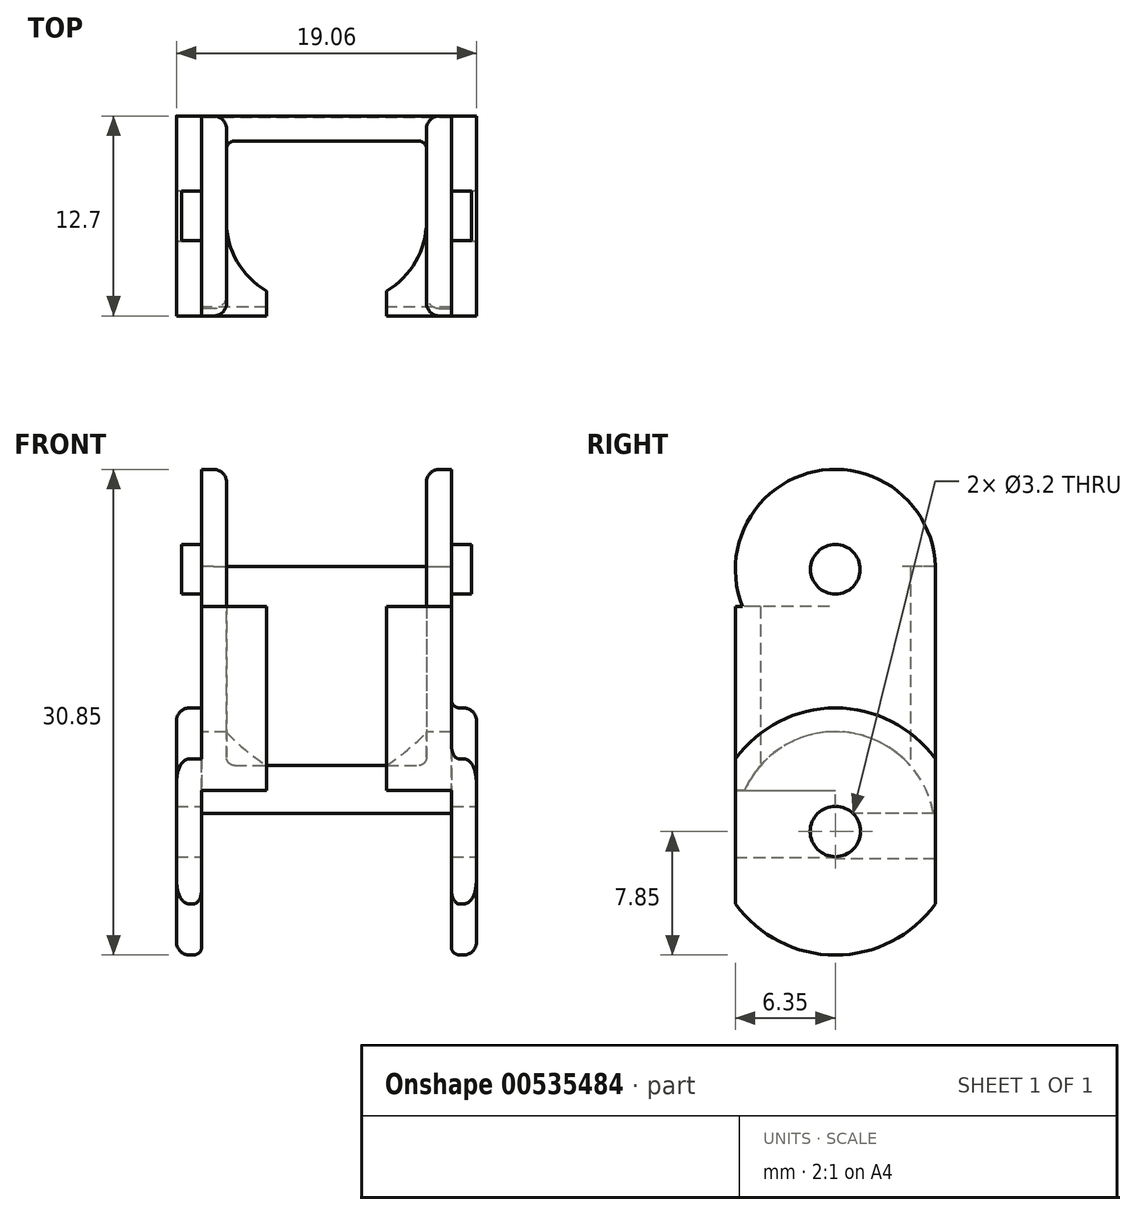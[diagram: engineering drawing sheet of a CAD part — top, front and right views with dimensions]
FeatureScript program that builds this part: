
annotation { "Feature Type Name" : "Feature", "Feature Type Description" : "" }
export const myFeature = defineFeature(function(context is Context, id is Id, definition is map)
    precondition{}
    {
        {
            var Q0;
            Q0=qCreatedBy(makeId("Top.planeOp"),FACE);
            var sketch = newSketch(context, id + "F0", { "sketchPlane" : qUnion([Q0])});
            skLineSegment(sketch, "E0.bottom", {"start": v(-7.94, 6.35) * mm, "end": v(7.94, 6.35) * mm});
            skLineSegment(sketch, "E0.top", {"start": v(-7.94, -6.35) * mm, "end": v(-3.81, -6.35) * mm});
            skLineSegment(sketch, "E0.left", {"start": v(-7.94, 6.35) * mm, "end": v(-7.94, -6.35) * mm});
            skLineSegment(sketch, "E0.right", {"start": v(7.94, 6.35) * mm, "end": v(7.94, -6.35) * mm});
            skPoint(sketch, "E0.middle", {"position": v(0, 0) * mm});
            skLineSegment(sketch, "E1.bottom", {"start": v(-6.35, 4.76) * mm, "end": v(6.35, 4.76) * mm});
            skLineSegment(sketch, "E1.top", {"start": v(-6.35, -4.76) * mm, "end": v(-3.81, -4.76) * mm});
            skLineSegment(sketch, "E1.left", {"start": v(-6.35, 4.76) * mm, "end": v(-6.35, -4.76) * mm});
            skLineSegment(sketch, "E1.right", {"start": v(6.35, 4.76) * mm, "end": v(6.35, -4.76) * mm});
            skLineSegment(sketch, "E2", {"start": v(-3.81, -4.76) * mm, "end": v(-3.81, -6.35) * mm});
            skLineSegment(sketch, "E3", {"start": v(3.81, -4.76) * mm, "end": v(3.81, -6.35) * mm});
            skLineSegment(sketch, "E4.trimOffspring", {"start": v(3.8, -6.35) * mm, "end": v(7.94, -6.35) * mm});
            skLineSegment(sketch, "E5.trimOffspring", {"start": v(3.8, -4.76) * mm, "end": v(6.35, -4.76) * mm});
            skSolve(sketch);
        }
        {
            var Q0;
            Q0=makeQuery(id+"F0.imprint","IMPRINT",FACE,{"disambiguationData":[TD([[makeQuery(id+"F0.imprint","IMPRINT",EDGE,{"derivedFrom":sQuery(id+"F0.wireOp",EDGE,"E0.bottom")}),-1.0]])]});
            extrude(context, id + "F1", {"entities" : qUnion([Q0]), "depth" : 14.29 * mm, "offsetDistance" : 25.4 * mm});
        }
        {
            var Q0;
            Q0=makeQuery(id+"F1.opExtrude","SWEPT_FACE",FACE,{"disambiguationData":[OSD([sQuery(id+"F0.wireOp",EDGE,"E0.right")])]});
            var sketch = newSketch(context, id + "F2", { "sketchPlane" : qUnion([Q0])});
            skCircle(sketch, "E6", {"center": v(0, 0) * mm, "radius": 6.35 * mm, "construction": true});
            skCircle(sketch, "E7", {"center": v(0, 16.65) * mm, "radius": 6.35 * mm});
            skSolve(sketch);
        }
        {
            var Q0;
            {var subQ1=sQuery(id+"F0.wireOp",EDGE,"E0.right");var subQ2=makeQuery(id+"F1.opExtrude","CAP_EDGE",EDGE,{"disambiguationData":[OSD([subQ1])],"isStart":false});Q0=makeQuery(id+"F2.imprint","IMPRINT",FACE,{"disambiguationData":[TD([[makeQuery(id+"F2.imprint","IMPRINT",EDGE,{"derivedFrom":subQ2}),-1.0]])]});}
            var Q1;
            Q1=makeQuery(id+"F1.opExtrude","SWEPT_FACE",FACE,{"disambiguationData":[OSD([sQuery(id+"F0.wireOp",EDGE,"E1.right")])]});
            extrude(context, id + "F3", {"entities" : qUnion([Q0]), "operationType" : NewBodyOperationType.ADD, "oppositeDirection" : true, "depth" : 1.59 * mm, "endBoundEntityFace" : qUnion([Q1]), "offsetDistance" : 25.4 * mm});
        }
        {
            var Q0;
            Q0=makeQuery(id+"F3.boolean.opBoolean","MERGE",FACE,{"derivedFrom":[makeQuery(id+"F1.opExtrude","SWEPT_FACE",FACE,{"disambiguationData":[OSD([sQuery(id+"F0.wireOp",EDGE,"E0.right")])]}),makeQuery(id+"F3.opExtrude","CAP_FACE",FACE,{"disambiguationData":[OSD([sQuery(id+"F2.wireOp",EDGE,"E7")])],"isStart":true})]});
            var sketch = newSketch(context, id + "F4", { "sketchPlane" : qUnion([Q0])});
            skCircle(sketch, "E8", {"center": v(0, 0) * mm, "radius": 7.85 * mm});
            skSolve(sketch);
        }
        {
            var Q0;
            Q0 = qSketchRegion(id + "F4", true);
            extrude(context, id + "F5", {"entities" : qUnion([Q0]), "operationType" : NewBodyOperationType.ADD, "depth" : 1.59 * mm, "offsetDistance" : 25.4 * mm});
        }
        {
            var Q0;
            Q0=makeQuery(id+"F1.opExtrude","SWEPT_BODY",BODY,{"disambiguationData":[OSD([sQuery(id+"F0.wireOp",EDGE,"E0.bottom"),sQuery(id+"F0.wireOp",EDGE,"E0.top"),sQuery(id+"F0.wireOp",EDGE,"E0.left"),sQuery(id+"F0.wireOp",EDGE,"E0.right"),sQuery(id+"F0.wireOp",EDGE,"E1.bottom"),sQuery(id+"F0.wireOp",EDGE,"E1.top"),sQuery(id+"F0.wireOp",EDGE,"E1.left"),sQuery(id+"F0.wireOp",EDGE,"E1.right"),sQuery(id+"F0.wireOp",EDGE,"E2"),sQuery(id+"F0.wireOp",EDGE,"E3"),sQuery(id+"F0.wireOp",EDGE,"E4.trimOffspring"),sQuery(id+"F0.wireOp",EDGE,"E5.trimOffspring")])]});
            var Q1;
            Q1=qCreatedBy(makeId("Right.planeOp"),FACE);
            mirror(context, id + "F6", {"operationType" : NewBodyOperationType.ADD, "entities" : qUnion([Q0]), "mirrorPlane" : qUnion([Q1])});
        }
        {
            var Q0;
            {var subQ0=sQuery(id+"F0.wireOp",EDGE,"E1.right");Q0=makeQuery(id+"F3.boolean.opBoolean","MERGE",FACE,{"derivedFrom":[makeQuery(id+"F1.opExtrude","SWEPT_FACE",FACE,{"disambiguationData":[OSD([subQ0])]}),makeQuery(id+"F3.opExtrude","CAP_FACE",FACE,{"disambiguationData":[OSD([subQ0])],"isStart":false})]});}
            var sketch = newSketch(context, id + "F7", { "sketchPlane" : qUnion([Q0])});
            skCircle(sketch, "E9", {"center": v(0, 0) * mm, "radius": 6.34 * mm});
            skSolve(sketch);
        }
        {
            var Q0;
            Q0 = qSketchRegion(id + "F7", true);
            var Q1;
            Q1=makeQuery(id+"F5.opExtrude","CAP_FACE",FACE,{"disambiguationData":[OSD([sQuery(id+"F4.wireOp",EDGE,"E8")])],"isStart":true});
            var Q2;
            Q2=makeQuery(id+"F6.opPattern","COPY",FACE,{"derivedFrom":makeQuery(id+"F5.opExtrude","CAP_FACE",FACE,{"disambiguationData":[OSD([sQuery(id+"F4.wireOp",EDGE,"E8")])],"isStart":true}),"instanceName":"1"});
            extrude(context, id + "F8", {"entities" : qUnion([Q0]), "operationType" : NewBodyOperationType.REMOVE, "endBound" : BoundingType.UP_TO_SURFACE, "oppositeDirection" : true, "depth" : 25.4 * mm, "endBoundEntityFace" : qUnion([Q1]), "offsetDistance" : 25.4 * mm, "hasSecondDirection" : true, "secondDirectionBound" : SecondDirectionBoundingType.UP_TO_SURFACE, "secondDirectionOppositeDirection" : false, "secondDirectionDepth" : 25.4 * mm, "secondDirectionBoundEntityFace" : qUnion([Q2])});
        }
        {
            var Q0;
            Q0=qCreatedBy(makeId("Front.planeOp"),FACE);
            var sketch = newSketch(context, id + "F9", { "sketchPlane" : qUnion([Q0])});
            skLineSegment(sketch, "E10.bottom", {"start": v(-7.94, 0) * mm, "end": v(7.94, 0) * mm});
            skLineSegment(sketch, "E10.top", {"start": v(-7.94, 5.88) * mm, "end": v(7.94, 5.88) * mm});
            skLineSegment(sketch, "E10.left", {"start": v(-7.94, 0) * mm, "end": v(-7.94, 5.88) * mm});
            skLineSegment(sketch, "E10.right", {"start": v(7.94, 0) * mm, "end": v(7.94, 5.88) * mm});
            skSolve(sketch);
        }
        {
            var Q0;
            Q0=makeQuery(id+"F5.opExtrude","CAP_EDGE",EDGE,{"disambiguationData":[OSD([sQuery(id+"F4.wireOp",EDGE,"E8")])],"isStart":false});
            var Q1;
            Q1=makeQuery(id+"F3.opExtrude","CAP_EDGE",EDGE,{"disambiguationData":[OSD([sQuery(id+"F2.wireOp",EDGE,"E7")])],"isStart":false});
            var Q2;
            Q2=makeQuery(id+"F6.opPattern","COPY",EDGE,{"derivedFrom":makeQuery(id+"F5.opExtrude","CAP_EDGE",EDGE,{"disambiguationData":[OSD([sQuery(id+"F4.wireOp",EDGE,"E8")])],"isStart":false}),"instanceName":"1"});
            var Q3;
            Q3=makeQuery(id+"F6.opPattern","COPY",EDGE,{"derivedFrom":makeQuery(id+"F3.opExtrude","CAP_EDGE",EDGE,{"disambiguationData":[OSD([sQuery(id+"F2.wireOp",EDGE,"E7")])],"isStart":false}),"instanceName":"1"});
            fillet(context, id + "F10", {"entities" : qUnion([Q0, Q1, Q2, Q3]), "radius" : 0.81 * mm, "tangentPropagation" : true, "allowEdgeOverflow" : false});
        }
        {
            var Q0;
            Q0 = qSketchRegion(id + "F7", true);
            extrude(context, id + "F11", {"entities" : qUnion([Q0]), "operationType" : NewBodyOperationType.REMOVE, "oppositeDirection" : true, "depth" : 1.59 * mm, "offsetDistance" : 25.4 * mm, "hasSecondDirection" : true, "secondDirectionOppositeDirection" : false, "secondDirectionDepth" : 14.29 * mm});
        }
        {
            var Q0;
            Q0=makeQuery(id+"F9.imprint","IMPRINT",FACE,{"disambiguationData":[TD([[makeQuery(id+"F9.imprint","IMPRINT",EDGE,{"derivedFrom":sQuery(id+"F9.wireOp",EDGE,"E10.bottom")}),1.0]])]});
            extrude(context, id + "F12", {"entities" : qUnion([Q0]), "operationType" : NewBodyOperationType.REMOVE, "endBound" : BoundingType.SYMMETRIC, "oppositeDirection" : true, "depth" : 25.4 * mm, "offsetDistance" : 25.4 * mm, "hasSecondDirection" : true, "secondDirectionOppositeDirection" : true, "secondDirectionDepth" : 25.4 * mm});
        }
        {
            var Q0;
            {var subQ1=sQuery(id+"F0.wireOp",EDGE,"E0.right");var subQ3=sQuery(id+"F0.wireOp",EDGE,"E1.bottom");var subQ5=sQuery(id+"F0.wireOp",EDGE,"E1.left");var subQ10=sQuery(id+"F0.wireOp",EDGE,"E0.left");var subQ12=sQuery(id+"F0.wireOp",EDGE,"E1.right");var subQ14=sQuery(id+"F0.wireOp",EDGE,"E0.bottom");var subQ15=makeQuery(id+"F1.opExtrude","SWEPT_FACE",FACE,{"disambiguationData":[OSD([subQ14])]});var subQ16=sQuery(id+"F0.wireOp",EDGE,"E2");var subQ17=sQuery(id+"F0.wireOp",EDGE,"E1.top");var subQ18=sQuery(id+"F0.wireOp",EDGE,"E0.top");Q0=makeQuery(id+"FmwXntm0pgXdfj9_1.boolean.opBoolean","SPLIT",FACE,{"disambiguationData":[TD([subQ15])],"derivedFrom":makeQuery(id+"F3.boolean.opBoolean","SPLIT",FACE,{"disambiguationData":[TD([subQ15])],"derivedFrom":makeQuery(id+"F1.opExtrude","CAP_FACE",FACE,{"disambiguationData":[OSD([subQ14,subQ18,subQ10,subQ1,subQ3,subQ17,subQ5,subQ12,subQ16,sQuery(id+"F0.wireOp",EDGE,"E3"),sQuery(id+"F0.wireOp",EDGE,"E4.trimOffspring"),sQuery(id+"F0.wireOp",EDGE,"E5.trimOffspring")])],"isStart":false})})});}
            var sketch = newSketch(context, id + "F13", { "sketchPlane" : qUnion([Q0])});
            skLineSegment(sketch, "E11.bottom", {"start": v(7.94, 4.76) * mm, "end": v(-7.94, 4.76) * mm});
            skLineSegment(sketch, "E11.top", {"start": v(7.94, 6.35) * mm, "end": v(-7.94, 6.35) * mm});
            skLineSegment(sketch, "E11.left", {"start": v(7.94, 4.76) * mm, "end": v(7.94, 6.35) * mm});
            skLineSegment(sketch, "E11.right", {"start": v(-7.94, 4.76) * mm, "end": v(-7.94, 6.35) * mm});
            skSolve(sketch);
        }
        {
            var Q0;
            Q0 = qSketchRegion(id + "F13", true);
            var Q1;
            {var subQ0=sQuery(id+"F7.wireOp",EDGE,"E9");var subQ2=sQuery(id+"F0.wireOp",EDGE,"E1.left");var subQ3=sQuery(id+"F0.wireOp",EDGE,"E2");var subQ6=sQuery(id+"F0.wireOp",EDGE,"E1.top");var subQ8=sQuery(id+"F0.wireOp",EDGE,"E0.bottom");var subQ9=sQuery(id+"F0.wireOp",EDGE,"E0.top");var subQ10=sQuery(id+"F0.wireOp",EDGE,"E0.left");var subQ11=sQuery(id+"F0.wireOp",EDGE,"E1.bottom");var subQ13=sQuery(id+"F0.wireOp",EDGE,"E5.trimOffspring");var subQ14=sQuery(id+"F0.wireOp",EDGE,"E4.trimOffspring");var subQ15=sQuery(id+"F0.wireOp",EDGE,"E3");var subQ16=makeQuery(id+"F1.opExtrude","CAP_FACE",FACE,{"disambiguationData":[OSD([subQ8,subQ9,subQ10,sQuery(id+"F0.wireOp",EDGE,"E0.right"),subQ11,subQ6,subQ2,sQuery(id+"F0.wireOp",EDGE,"E1.right"),subQ3,subQ15,subQ14,subQ13])],"isStart":true});var subQ17=makeQuery(id+"F8.boolean.opBoolean","SPLIT",FACE,{"disambiguationData":[TD([makeQuery(id+"F1.opExtrude","SWEPT_FACE",FACE,{"disambiguationData":[OSD([subQ8])]})])],"derivedFrom":subQ16});Q1=makeQuery(id+"F11.boolean.opBoolean","INTERSECT",VERTEX,{"disambiguationData":[OD(0.0)],"derivedFrom":[makeQuery(id+"FmwXntm0pgXdfj9_1.boolean.opBoolean","MERGE",FACE,{"derivedFrom":[subQ17,makeQuery(id+"F8.boolean.opBoolean","SPLIT",FACE,{"disambiguationData":[TD([makeQuery(id+"F1.opExtrude","SWEPT_FACE",FACE,{"disambiguationData":[OSD([subQ15])]})])],"derivedFrom":subQ16}),makeQuery(id+"FmwXntm0pgXdfj9_1.opPattern","COPY",FACE,{"derivedFrom":subQ17,"instanceName":"1"})]}),makeQuery(id+"F11.opExtrude","SWEPT_FACE",FACE,{"disambiguationData":[OSD([subQ0])]})]});}
            extrude(context, id + "F14", {"entities" : qUnion([Q0]), "operationType" : NewBodyOperationType.ADD, "depth" : 2.54 * mm, "endBoundEntityVertex" : qUnion([Q1]), "offsetDistance" : 25.4 * mm});
        }
        {
            var Q0;
            {var subQ0=sQuery(id+"F4.wireOp",EDGE,"E8");Q0=makeQuery(id+"F4vwekiissYTjzZ_1.boolean.opBoolean","MERGE",FACE,{"derivedFrom":[makeQuery(id+"F12.boolean.opBoolean","MERGE",FACE,{"derivedFrom":[makeQuery(id+"F11.boolean.opBoolean","MERGE",FACE,{"derivedFrom":[makeQuery(id+"F8.boolean.opBoolean","MERGE",FACE,{"derivedFrom":[makeQuery(id+"F5.opExtrude","CAP_FACE",FACE,{"disambiguationData":[OSD([subQ0])],"isStart":true}),makeQuery(id+"F8.opExtrude","CAP_FACE",FACE,{"disambiguationData":[OSD([subQ0])],"isStart":false})]}),makeQuery(id+"F11.opExtrude","CAP_FACE",FACE,{"disambiguationData":[OSD([sQuery(id+"F7.wireOp",EDGE,"E9")])],"isStart":false})]}),makeQuery(id+"F12.opExtrude","SWEPT_FACE",FACE,{"disambiguationData":[OSD([sQuery(id+"F9.wireOp",EDGE,"E10.right")])]})]}),makeQuery(id+"F4vwekiissYTjzZ_1.opExtrude","CAP_FACE",FACE,{"disambiguationData":[OSD([sQuery(id+"F27.wireOp",EDGE,"E23")])],"isStart":true})]});}
            var sketch = newSketch(context, id + "F15", { "sketchPlane" : qUnion([Q0])});
            skCircle(sketch, "E12", {"center": v(0, 0) * mm, "radius": 1.6 * mm});
            skSolve(sketch);
        }
        {
            var Q0;
            Q0 = qSketchRegion(id + "F15", true);
            extrude(context, id + "F16", {"entities" : qUnion([Q0]), "operationType" : NewBodyOperationType.REMOVE, "depth" : 25.4 * mm, "offsetDistance" : 25.4 * mm, "hasSecondDirection" : true, "secondDirectionOppositeDirection" : true, "secondDirectionDepth" : 25.4 * mm});
        }
        {
            var Q0;
            {var subQ0=sQuery(id+"F0.wireOp",EDGE,"E0.right");Q0=makeQuery(id+"FuRak2iaO5MuixO_1.boolean.opBoolean","MERGE",FACE,{"derivedFrom":[makeQuery(id+"F14.boolean.opBoolean","MERGE",FACE,{"derivedFrom":[makeQuery(id+"F3.boolean.opBoolean","MERGE",FACE,{"derivedFrom":[makeQuery(id+"F1.opExtrude","SWEPT_FACE",FACE,{"disambiguationData":[OSD([subQ0])]}),makeQuery(id+"F3.opExtrude","CAP_FACE",FACE,{"disambiguationData":[OSD([subQ0,sQuery(id+"F2.wireOp",EDGE,"E7")])],"isStart":true})]}),makeQuery(id+"F14.opExtrude","SWEPT_FACE",FACE,{"disambiguationData":[OSD([sQuery(id+"F9.wireOp",EDGE,"E10.top"),sQuery(id+"F9.wireOp",EDGE,"E10.right")])]})]}),makeQuery(id+"FuRak2iaO5MuixO_1.opExtrude","SWEPT_FACE",FACE,{"disambiguationData":[OSD([sQuery(id+"F13.wireOp",EDGE,"E11.left")])]})]});}
            var sketch = newSketch(context, id + "F17", { "sketchPlane" : qUnion([Q0])});
            skCircle(sketch, "E13", {"center": v(0, 16.65) * mm, "radius": 1.57 * mm});
            skSolve(sketch);
        }
        {
            var Q0;
            Q0=makeQuery(id+"F17.imprint","IMPRINT",FACE,{"disambiguationData":[TD([[makeQuery(id+"F17.imprint","IMPRINT",EDGE,{"derivedFrom":sQuery(id+"F17.wireOp",EDGE,"E13")}),1.0]])]});
            extrude(context, id + "F18", {"entities" : qUnion([Q0]), "operationType" : NewBodyOperationType.ADD, "depth" : 1.27 * mm, "offsetDistance" : 25.4 * mm});
        }
        {
            var Q0;
            {var subQ0=sQuery(id+"F0.wireOp",EDGE,"E0.right");var subQ1=makeQuery(id+"FmwXntm0pgXdfj9_1.opPattern","COPY",FACE,{"derivedFrom":makeQuery(id+"F3.boolean.opBoolean","MERGE",FACE,{"derivedFrom":[makeQuery(id+"F1.opExtrude","SWEPT_FACE",FACE,{"disambiguationData":[OSD([subQ0])]}),makeQuery(id+"F3.opExtrude","CAP_FACE",FACE,{"disambiguationData":[OSD([subQ0,sQuery(id+"F2.wireOp",EDGE,"E7")])],"isStart":true})]}),"instanceName":"1"});var subQ2=makeQuery(id+"F1.opExtrude","SWEPT_FACE",FACE,{"disambiguationData":[OSD([sQuery(id+"F0.wireOp",EDGE,"E0.left")])]});var subQ3=sQuery(id+"F9.wireOp",EDGE,"E10.left");var subQ4=sQuery(id+"F9.wireOp",EDGE,"E10.top");var subQ5=makeQuery(id+"F12.opExtrude","SWEPT_FACE",FACE,{"disambiguationData":[OSD([subQ4])]});Q0=makeQuery(id+"FuRak2iaO5MuixO_1.boolean.opBoolean","MERGE",FACE,{"derivedFrom":[makeQuery(id+"F14.boolean.opBoolean","MERGE",FACE,{"derivedFrom":[makeQuery(id+"FmwXntm0pgXdfj9_1.boolean.opBoolean","MERGE",FACE,{"derivedFrom":[subQ2,subQ1]}),makeQuery(id+"F14.opExtrude","SWEPT_FACE",FACE,{"disambiguationData":[OSD([subQ4,subQ3]),TDD([makeQuery(id+"F12.boolean.opBoolean","COPY",EDGE,{"disambiguationData":[topologyDisambiguationEdgeConnected([subQ2,subQ1,subQ5]),TD([makeQuery(id+"F1.opExtrude","SWEPT_FACE",FACE,{"disambiguationData":[OSD([sQuery(id+"F0.wireOp",EDGE,"E0.bottom")])]})])],"derivedFrom":makeQuery(id+"F12.opExtrude","SWEPT_EDGE",EDGE,{"disambiguationData":[OSD([subQ4,subQ3])]})})])]})]}),makeQuery(id+"FuRak2iaO5MuixO_1.opExtrude","SWEPT_FACE",FACE,{"disambiguationData":[OSD([sQuery(id+"F13.wireOp",EDGE,"E11.right")])]})]});}
            var sketch = newSketch(context, id + "F19", { "sketchPlane" : qUnion([Q0])});
            skCircle(sketch, "E14", {"center": v(0, 16.65) * mm, "radius": 1.57 * mm});
            skSolve(sketch);
        }
        {
            var Q0;
            Q0 = qSketchRegion(id + "F19", true);
            extrude(context, id + "F20", {"entities" : qUnion([Q0]), "operationType" : NewBodyOperationType.ADD, "depth" : 1.27 * mm, "offsetDistance" : 25.4 * mm});
        }
        {
            var Q0;
            Q0=makeQuery(id+"F12.boolean.opBoolean","COPY",FACE,{"disambiguationData":[TD([makeQuery(id+"F1.opExtrude","SWEPT_FACE",FACE,{"disambiguationData":[OSD([sQuery(id+"F0.wireOp",EDGE,"E0.bottom")])]})])],"derivedFrom":makeQuery(id+"F12.opExtrude","SWEPT_FACE",FACE,{"disambiguationData":[OSD([sQuery(id+"F9.wireOp",EDGE,"E10.top")])]})});
            var Q1;
            Q1=makeQuery(id+"F14.opExtrude","CAP_VERTEX",VERTEX,{"disambiguationData":[OSD([sQuery(id+"F0.wireOp",EDGE,"E0.bottom"),sQuery(id+"F9.wireOp",EDGE,"E10.top"),sQuery(id+"F9.wireOp",EDGE,"E10.right"),dummyQuery(id+"F14.vertexPlane.planeOp",FACE)])],"isStart":false});
            extrude(context, id + "F21", {"entities" : qUnion([Q0]), "operationType" : NewBodyOperationType.ADD, "depth" : 5.08 * mm, "endBoundEntityVertex" : qUnion([Q1]), "offsetDistance" : 25.4 * mm});
        }
        {
            var Q0;
            Q0=makeQuery(id+"F1.opExtrude","SWEPT_EDGE",EDGE,{"disambiguationData":[OSD([sQuery(id+"F0.wireOp",EDGE,"E1.top"),sQuery(id+"F0.wireOp",EDGE,"E1.left")])]});
            fillet(context, id + "F22", {"entities" : qUnion([Q0]), "radius" : 5.08 * mm, "tangentPropagation" : true, "allowEdgeOverflow" : false});
        }
        {
            var Q0;
            {var subQ0=sQuery(id+"F0.wireOp",EDGE,"E5.trimOffspring");var subQ2=sQuery(id+"F0.wireOp",EDGE,"E1.right");var subQ3=makeQuery(id+"F1.opExtrude","SWEPT_EDGE",EDGE,{"disambiguationData":[OSD([subQ2,subQ0])]});Q0=makeQuery(id+"FmwXntm0pgXdfj9_1.boolean.opBoolean","MERGE",EDGE,{"derivedFrom":[makeQuery(id+"F8.boolean.opBoolean","SPLIT",EDGE,{"disambiguationData":[topologyDisambiguationEdgeConnected([makeQuery(id+"F1.opExtrude","SWEPT_FACE",FACE,{"disambiguationData":[OSD([subQ2])]})])],"derivedFrom":subQ3}),makeQuery(id+"F8.boolean.opBoolean","SPLIT",EDGE,{"disambiguationData":[topologyDisambiguationEdgeConnected([makeQuery(id+"F8.opExtrude","CAP_FACE",FACE,{"disambiguationData":[OSD([sQuery(id+"F7.wireOp",EDGE,"E9")])],"isStart":true})])],"derivedFrom":subQ3}),makeQuery(id+"FmwXntm0pgXdfj9_1.opPattern","COPY",EDGE,{"derivedFrom":makeQuery(id+"F1.opExtrude","SWEPT_EDGE",EDGE,{"disambiguationData":[OSD([sQuery(id+"F0.wireOp",EDGE,"E1.top"),sQuery(id+"F0.wireOp",EDGE,"E1.left")])]}),"instanceName":"1"})]});}
            fillet(context, id + "F23", {"entities" : qUnion([Q0]), "radius" : 5.08 * mm, "tangentPropagation" : true, "allowEdgeOverflow" : false});
        }
        {
            var Q0;
            {var subQ0=sQuery(id+"F0.wireOp",EDGE,"E0.right");var subQ1=makeQuery(id+"FmwXntm0pgXdfj9_1.opPattern","COPY",FACE,{"derivedFrom":makeQuery(id+"F3.boolean.opBoolean","MERGE",FACE,{"derivedFrom":[makeQuery(id+"F1.opExtrude","SWEPT_FACE",FACE,{"disambiguationData":[OSD([subQ0])]}),makeQuery(id+"F3.opExtrude","CAP_FACE",FACE,{"disambiguationData":[OSD([subQ0,sQuery(id+"F2.wireOp",EDGE,"E7")])],"isStart":true})]}),"instanceName":"1"});var subQ2=makeQuery(id+"F1.opExtrude","SWEPT_FACE",FACE,{"disambiguationData":[OSD([sQuery(id+"F0.wireOp",EDGE,"E0.left")])]});var subQ3=sQuery(id+"F9.wireOp",EDGE,"E10.left");var subQ4=sQuery(id+"F9.wireOp",EDGE,"E10.top");var subQ5=makeQuery(id+"F12.opExtrude","SWEPT_FACE",FACE,{"disambiguationData":[OSD([subQ4])]});Q0=makeQuery(id+"FuRak2iaO5MuixO_1.boolean.opBoolean","MERGE",FACE,{"derivedFrom":[makeQuery(id+"F14.boolean.opBoolean","MERGE",FACE,{"derivedFrom":[makeQuery(id+"FmwXntm0pgXdfj9_1.boolean.opBoolean","MERGE",FACE,{"derivedFrom":[subQ2,subQ1]}),makeQuery(id+"F14.opExtrude","SWEPT_FACE",FACE,{"disambiguationData":[OSD([subQ4,subQ3]),TDD([makeQuery(id+"F12.boolean.opBoolean","COPY",EDGE,{"disambiguationData":[topologyDisambiguationEdgeConnected([subQ2,subQ1,subQ5]),TD([makeQuery(id+"F1.opExtrude","SWEPT_FACE",FACE,{"disambiguationData":[OSD([sQuery(id+"F0.wireOp",EDGE,"E0.bottom")])]})])],"derivedFrom":makeQuery(id+"F12.opExtrude","SWEPT_EDGE",EDGE,{"disambiguationData":[OSD([subQ4,subQ3])]})})])]})]}),makeQuery(id+"FuRak2iaO5MuixO_1.opExtrude","SWEPT_FACE",FACE,{"disambiguationData":[OSD([sQuery(id+"F13.wireOp",EDGE,"E11.right")])]})]});}
            var sketch = newSketch(context, id + "F24", { "sketchPlane" : qUnion([Q0])});
            skLineSegment(sketch, "E15", {"start": v(-6.35, 5.88) * mm, "end": v(-6.35, -9.42) * mm});
            skLineSegment(sketch, "E16", {"start": v(-6.35, -9.42) * mm, "end": v(6.35, -9.42) * mm});
            skLineSegment(sketch, "E17", {"start": v(6.35, 5.88) * mm, "end": v(6.35, -9.42) * mm});
            skLineSegment(sketch, "E18", {"start": v(6.35, 5.88) * mm, "end": v(10.23, 5.88) * mm});
            skLineSegment(sketch, "E19", {"start": v(10.23, 5.88) * mm, "end": v(10.23, -12.67) * mm});
            skLineSegment(sketch, "E20", {"start": v(10.23, -12.67) * mm, "end": v(-9.62, -12.67) * mm});
            skLineSegment(sketch, "E21", {"start": v(-9.62, -12.67) * mm, "end": v(-9.62, 5.69) * mm});
            skLineSegment(sketch, "E22", {"start": v(-9.62, 5.69) * mm, "end": v(-6.35, 5.88) * mm});
            skSolve(sketch);
        }
        {
            var Q0;
            {var subQ0=sQuery(id+"F24.wireOp",EDGE,"E16");Q0=makeQuery(id+"F24.imprint","IMPRINT",FACE,{"disambiguationData":[TD([[makeQuery(id+"F24.imprint","IMPRINT",EDGE,{"derivedFrom":subQ0}),-1.0]])]});}
            var Q1;
            Q1=makeQuery(id+"F6.opPattern","COPY",FACE,{"derivedFrom":makeQuery(id+"F5.opExtrude","CAP_FACE",FACE,{"disambiguationData":[OSD([sQuery(id+"F4.wireOp",EDGE,"E8")])],"isStart":false}),"instanceName":"1"});
            extrude(context, id + "F25", {"entities" : qUnion([Q0]), "operationType" : NewBodyOperationType.REMOVE, "endBound" : BoundingType.UP_TO_SURFACE, "depth" : 25.4 * mm, "endBoundEntityFace" : qUnion([Q1]), "offsetDistance" : 25.4 * mm, "hasSecondDirection" : true, "secondDirectionOppositeDirection" : true, "secondDirectionDepth" : 25.4 * mm});
        }
        {
            var Q0;
            Q0=makeQuery(id+"F12.boolean.opBoolean","COPY",FACE,{"disambiguationData":[TD([makeQuery(id+"F1.opExtrude","SWEPT_FACE",FACE,{"disambiguationData":[OSD([sQuery(id+"F0.wireOp",EDGE,"E3")])]})])],"derivedFrom":makeQuery(id+"F12.opExtrude","SWEPT_FACE",FACE,{"disambiguationData":[OSD([sQuery(id+"F9.wireOp",EDGE,"E10.top")])]})});
            var Q1;
            Q1=makeQuery(id+"F12.boolean.opBoolean","COPY",FACE,{"disambiguationData":[TD([makeQuery(id+"F1.opExtrude","SWEPT_FACE",FACE,{"disambiguationData":[OSD([sQuery(id+"F0.wireOp",EDGE,"E0.top")])]})])],"derivedFrom":makeQuery(id+"F12.opExtrude","SWEPT_FACE",FACE,{"disambiguationData":[OSD([sQuery(id+"F9.wireOp",EDGE,"E10.top")])]})});
            var Q2;
            Q2=makeQuery(id+"F21.opExtrude","CAP_FACE",FACE,{"disambiguationData":[OSD([sQuery(id+"F9.wireOp",EDGE,"E10.top")])],"isStart":false});
            extrude(context, id + "F26", {"entities" : qUnion([Q0, Q1]), "operationType" : NewBodyOperationType.ADD, "endBound" : BoundingType.UP_TO_SURFACE, "depth" : 25.4 * mm, "endBoundEntityFace" : qUnion([Q2]), "offsetDistance" : 25.4 * mm});
        }
        {
            var Q0;
            {var subQ0=sQuery(id+"F4.wireOp",EDGE,"E8");Q0=makeQuery(id+"F12.boolean.opBoolean","MERGE",FACE,{"derivedFrom":[makeQuery(id+"F11.boolean.opBoolean","MERGE",FACE,{"derivedFrom":[makeQuery(id+"F8.boolean.opBoolean","MERGE",FACE,{"derivedFrom":[makeQuery(id+"F5.opExtrude","CAP_FACE",FACE,{"disambiguationData":[OSD([subQ0])],"isStart":true}),makeQuery(id+"F8.opExtrude","CAP_FACE",FACE,{"disambiguationData":[OSD([subQ0])],"isStart":false})]}),makeQuery(id+"F11.opExtrude","CAP_FACE",FACE,{"disambiguationData":[OSD([sQuery(id+"F7.wireOp",EDGE,"E9")])],"isStart":false})]}),makeQuery(id+"F12.opExtrude","SWEPT_FACE",FACE,{"disambiguationData":[OSD([sQuery(id+"F9.wireOp",EDGE,"E10.right")])]})]});}
            var sketch = newSketch(context, id + "F27", { "sketchPlane" : qUnion([Q0])});
            skCircle(sketch, "E23", {"center": v(0, 0) * mm, "radius": 6.34 * mm});
            skSolve(sketch);
        }
        {
            var Q0;
            Q0 = qSketchRegion(id + "F27", true);
            var Q1;
            {var subQ0=sQuery(id+"F4.wireOp",EDGE,"E8");Q1=makeQuery(id+"F8.boolean.opBoolean","MERGE",FACE,{"derivedFrom":[makeQuery(id+"F6.opPattern","COPY",FACE,{"derivedFrom":makeQuery(id+"F5.opExtrude","CAP_FACE",FACE,{"disambiguationData":[OSD([subQ0])],"isStart":true}),"instanceName":"1"}),makeQuery(id+"F8.opExtrude","CAP_FACE",FACE,{"disambiguationData":[OSD([subQ0])],"isStart":true})]});}
            extrude(context, id + "F28", {"entities" : qUnion([Q0]), "operationType" : NewBodyOperationType.REMOVE, "endBound" : BoundingType.UP_TO_SURFACE, "depth" : 25.4 * mm, "endBoundEntityFace" : qUnion([Q1]), "offsetDistance" : 25.4 * mm});
        }
        {
            var Q0;
            {var subQ0=sQuery(id+"F0.wireOp",EDGE,"E0.right");var subQ1=sQuery(id+"F4.wireOp",EDGE,"E8");Q0=makeQuery(id+"F12.boolean.opBoolean","SPLIT",EDGE,{"derivedFrom":makeQuery(id+"F5.boolean.opBoolean","SPLIT",EDGE,{"disambiguationData":[topologyDisambiguationEdgeConnected([makeQuery(id+"F1.opExtrude","SWEPT_FACE",FACE,{"disambiguationData":[OSD([subQ0])]})])],"derivedFrom":makeQuery(id+"F5.opExtrude","CAP_EDGE",EDGE,{"disambiguationData":[OSD([subQ1])],"isStart":true})})});}
            var Q1;
            {var subQ0=sQuery(id+"F4.wireOp",EDGE,"E8");var subQ1=makeQuery(id+"F5.opExtrude","SWEPT_FACE",FACE,{"disambiguationData":[OSD([subQ0])]});var subQ2=sQuery(id+"F0.wireOp",EDGE,"E0.right");var subQ3=makeQuery(id+"F3.opExtrude","CAP_FACE",FACE,{"disambiguationData":[OSD([subQ2,sQuery(id+"F2.wireOp",EDGE,"E7")])],"isStart":true});var subQ4=makeQuery(id+"F1.opExtrude","SWEPT_FACE",FACE,{"disambiguationData":[OSD([subQ2])]});Q1=makeQuery(id+"F12.boolean.opBoolean","SPLIT",EDGE,{"disambiguationData":[topologyDisambiguationEdgeConnected([makeQuery(id+"F1.opExtrude","SWEPT_FACE",FACE,{"disambiguationData":[OSD([sQuery(id+"F0.wireOp",EDGE,"E0.left")])]}),makeQuery(id+"F6.opPattern","COPY",FACE,{"derivedFrom":subQ1,"instanceName":"1"}),makeQuery(id+"F6.opPattern","COPY",FACE,{"derivedFrom":makeQuery(id+"F3.boolean.opBoolean","MERGE",FACE,{"derivedFrom":[subQ4,subQ3]}),"instanceName":"1"})])],"derivedFrom":makeQuery(id+"F6.opPattern","COPY",EDGE,{"derivedFrom":makeQuery(id+"F5.boolean.opBoolean","SPLIT",EDGE,{"disambiguationData":[topologyDisambiguationEdgeConnected([subQ4])],"derivedFrom":makeQuery(id+"F5.opExtrude","CAP_EDGE",EDGE,{"disambiguationData":[OSD([subQ0])],"isStart":true})}),"instanceName":"1"})});}
            fillet(context, id + "F29", {"entities" : qUnion([Q0, Q1]), "radius" : 0.5 * mm, "tangentPropagation" : true, "allowEdgeOverflow" : false});
        }
        {
            var Q0;
            Q0=qCreatedBy(makeId("Front.planeOp"),FACE);
            var sketch = newSketch(context, id + "F30", { "sketchPlane" : qUnion([Q0])});
            skLineSegment(sketch, "E24.bottom", {"start": v(-7.95, -1.65) * mm, "end": v(7.95, -1.65) * mm});
            skLineSegment(sketch, "E24.top", {"start": v(-7.95, 2.61) * mm, "end": v(7.95, 2.61) * mm});
            skLineSegment(sketch, "E24.left", {"start": v(-7.95, -1.65) * mm, "end": v(-7.95, 2.61) * mm});
            skLineSegment(sketch, "E24.right", {"start": v(7.95, -1.65) * mm, "end": v(7.95, 2.61) * mm});
            skSolve(sketch);
        }
        {
            var Q0;
            Q0 = qSketchRegion(id + "F30", true);
            extrude(context, id + "F31", {"entities" : qUnion([Q0]), "operationType" : NewBodyOperationType.REMOVE, "depth" : 25.4 * mm, "offsetDistance" : 25.4 * mm});
        }
        {
            var Q0;
            Q0=qCreatedBy(makeId("Front.planeOp"),FACE);
            var sketch = newSketch(context, id + "F32", { "sketchPlane" : qUnion([Q0])});
            skLineSegment(sketch, "E25.bottom", {"start": v(-7.97, -1.73) * mm, "end": v(7.95, -1.73) * mm});
            skLineSegment(sketch, "E25.top", {"start": v(-7.97, 1.14) * mm, "end": v(7.95, 1.14) * mm});
            skLineSegment(sketch, "E25.left", {"start": v(-7.97, -1.73) * mm, "end": v(-7.97, 1.14) * mm});
            skLineSegment(sketch, "E25.right", {"start": v(7.95, -1.73) * mm, "end": v(7.95, 1.14) * mm});
            skSolve(sketch);
        }
        {
            var Q0;
            Q0=makeQuery(id+"F32.imprint","IMPRINT",FACE,{"disambiguationData":[TD([[makeQuery(id+"F32.imprint","IMPRINT",EDGE,{"derivedFrom":sQuery(id+"F32.wireOp",EDGE,"E25.bottom")}),1.0]])]});
            extrude(context, id + "F33", {"entities" : qUnion([Q0]), "operationType" : NewBodyOperationType.REMOVE, "oppositeDirection" : true, "depth" : 15.24 * mm, "offsetDistance" : 25.4 * mm});
        }
        {
            var Q0;
            {var subQ0=sQuery(id+"F2.wireOp",EDGE,"E7");var subQ1=sQuery(id+"F0.wireOp",EDGE,"E1.right");var subQ2=sQuery(id+"F0.wireOp",EDGE,"E0.right");Q0=makeQuery(id+"F21.boolean.opBoolean","MERGE",EDGE,{"derivedFrom":[makeQuery(id+"F14.boolean.opBoolean","INTERSECT",EDGE,{"derivedFrom":[makeQuery(id+"F3.boolean.opBoolean","MERGE",FACE,{"derivedFrom":[makeQuery(id+"F1.opExtrude","SWEPT_FACE",FACE,{"disambiguationData":[OSD([subQ1])]}),makeQuery(id+"F3.opExtrude","CAP_FACE",FACE,{"disambiguationData":[OSD([subQ2,subQ0])],"isStart":false})]}),makeQuery(id+"F14.opExtrude","SWEPT_FACE",FACE,{"disambiguationData":[OSD([sQuery(id+"F13.wireOp",EDGE,"E11.bottom")])]})]}),makeQuery(id+"F21.opExtrude","SWEPT_EDGE",EDGE,{"disambiguationData":[OSD([subQ2,sQuery(id+"F0.wireOp",EDGE,"E1.bottom"),subQ1,subQ0,sQuery(id+"F9.wireOp",EDGE,"E10.top")])]})]});}
            var Q1;
            {var subQ0=sQuery(id+"F2.wireOp",EDGE,"E7");var subQ1=sQuery(id+"F0.wireOp",EDGE,"E1.right");var subQ2=sQuery(id+"F0.wireOp",EDGE,"E1.left");var subQ3=sQuery(id+"F0.wireOp",EDGE,"E0.right");Q1=makeQuery(id+"F21.boolean.opBoolean","MERGE",EDGE,{"derivedFrom":[makeQuery(id+"F14.boolean.opBoolean","INTERSECT",EDGE,{"derivedFrom":[makeQuery(id+"F6.boolean.opBoolean","MERGE",FACE,{"derivedFrom":[makeQuery(id+"F1.opExtrude","SWEPT_FACE",FACE,{"disambiguationData":[OSD([subQ2])]}),makeQuery(id+"F6.opPattern","COPY",FACE,{"derivedFrom":makeQuery(id+"F3.boolean.opBoolean","MERGE",FACE,{"derivedFrom":[makeQuery(id+"F1.opExtrude","SWEPT_FACE",FACE,{"disambiguationData":[OSD([subQ1])]}),makeQuery(id+"F3.opExtrude","CAP_FACE",FACE,{"disambiguationData":[OSD([subQ3,subQ0])],"isStart":false})]}),"instanceName":"1"})]}),makeQuery(id+"F14.opExtrude","SWEPT_FACE",FACE,{"disambiguationData":[OSD([sQuery(id+"F13.wireOp",EDGE,"E11.bottom")])]})]}),makeQuery(id+"F21.opExtrude","SWEPT_EDGE",EDGE,{"disambiguationData":[OSD([subQ3,sQuery(id+"F0.wireOp",EDGE,"E1.bottom"),subQ2,subQ1,subQ0,sQuery(id+"F9.wireOp",EDGE,"E10.top")])]})]});}
            fillet(context, id + "F34", {"entities" : qUnion([Q0, Q1]), "radius" : 0.5 * mm, "tangentPropagation" : true, "allowEdgeOverflow" : false});
        }
    });
